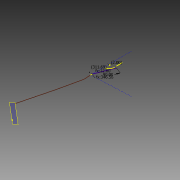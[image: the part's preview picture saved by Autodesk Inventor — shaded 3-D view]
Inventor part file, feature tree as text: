
AUTODESK INVENTOR PART (.ipt)
format: ipt  version: 2020 (Build 240168000, 168)  size: 167,424 bytes
history: native  units: mm
features: reference x10, other x9, sketch x4, plane x2, sweep x2, projected_geometry x2
ambient origin geometry x8: Origin, YZ Plane, XZ Plane, XY Plane, X Axis, Y Axis, Z Axis, Center Point
bodies: Solid1 (feature_tree), Solid2 (feature_tree)
feature tree (29):
  sketch  "Sketch1"  dims[d0=498.0mm d1=3.0mm]
  plane  "Work Plane1"
  sweep  "Sweep1"
  plane  "Work Plane2"
  sweep  "Sweep2"
  reference  "Reference1"
  reference  "Reference2"
  reference  "Reference3"
  reference  "Reference4"
  reference  "Reference5"
  reference  "Reference6"
  reference  "Reference7"
  other  "Work Point1"
  sketch  "Sketch2"  dims[d2=3.0mm d4=3.0mm]
  sketch  "Sketch3"  dims[d7=6.0mm]
  projected_geometry  "Projected Loop1"
  reference  "Reference8"
  reference  "Reference9"
  sketch  "Sketch4"  dims[d9=6.0mm d10=0.0mm d11=0.0mm d12=90.0deg d13=45.378561mm d14=4.479678mm d16=497.477531mm d17=0.0mm d18=0.0mm]
  reference  "Reference10"
  projected_geometry  "Projected Loop2"
  other  "1000_Planar Winding Jig Overall Assembly_V1.iam"
  other  "12111_Proximal Roller_V1:1"
  other  "12111_Proximal Roller_V1:2"
  other  "1219_Middle Roller_V1:1"
  other  "1213_Distal Roller_V1:1"
  other  "1312_Former Middle_V1:1"
  other  "1213_Distal Roller_V1:2"
  other  "1240_Wire Spool and Wire:1"
